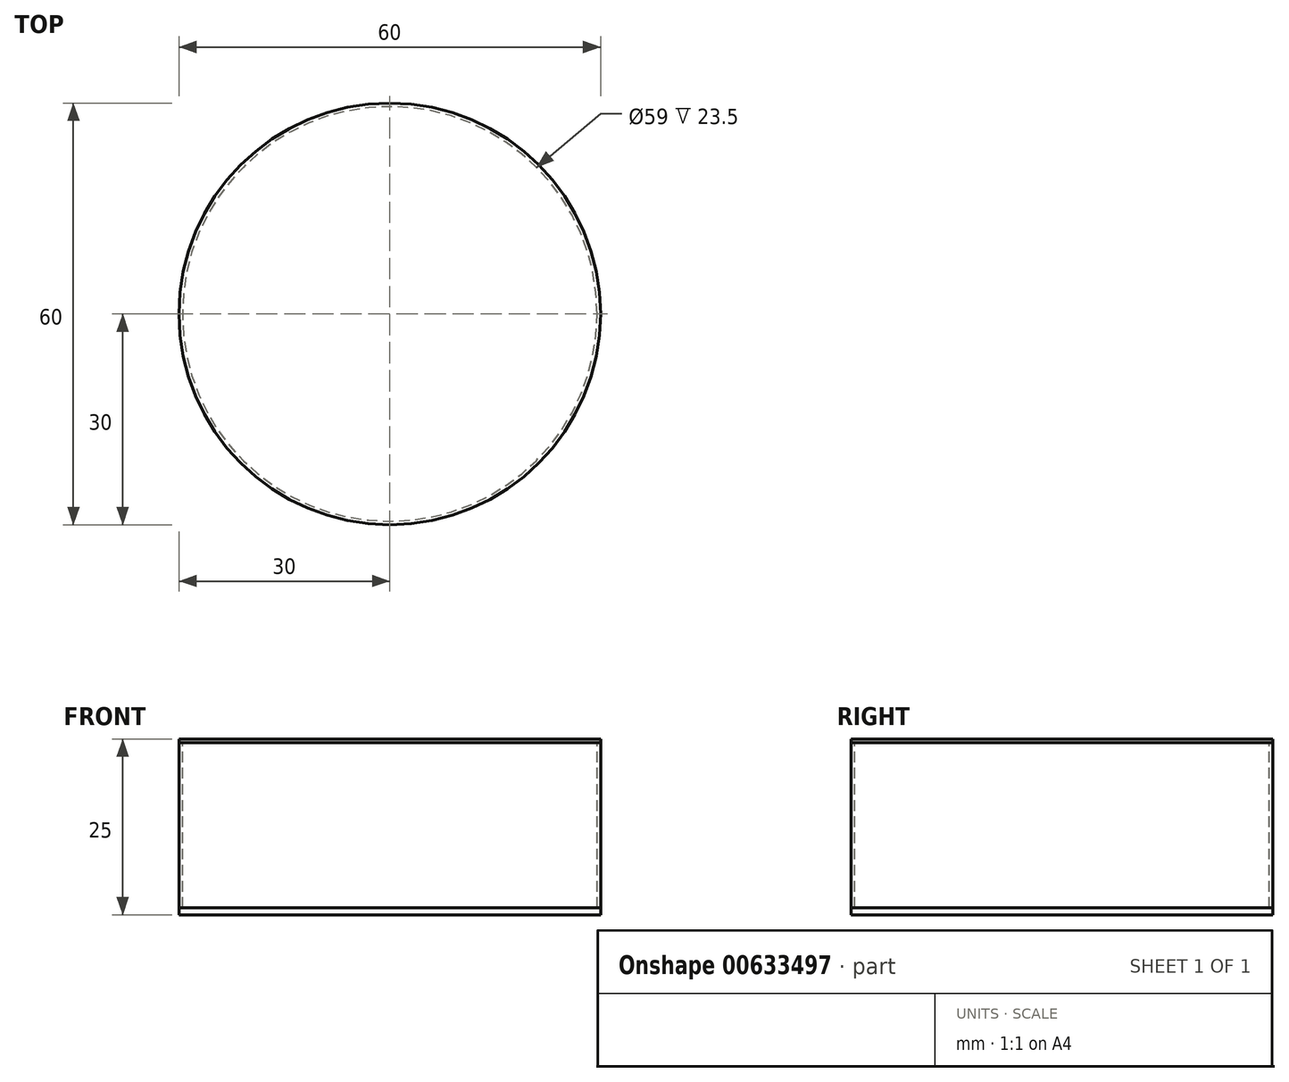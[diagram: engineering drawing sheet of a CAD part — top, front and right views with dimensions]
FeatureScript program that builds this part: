
annotation { "Feature Type Name" : "Feature", "Feature Type Description" : "" }
export const myFeature = defineFeature(function(context is Context, id is Id, definition is map)
    precondition{}
    {
        {
            var Q0;
            Q0=qCreatedBy(makeId("Top.planeOp"),FACE);
            var sketch = newSketch(context, id + "F0", { "sketchPlane" : qUnion([Q0])});
            skCircle(sketch, "E0", {"center": v(0, 0) * mm, "radius": 30 * mm});
            skSolve(sketch);
        }
        {
            var Q0;
            Q0=makeQuery(id+"F0.imprint","IMPRINT",FACE,{"disambiguationData":[TD([[makeQuery(id+"F0.imprint","IMPRINT",EDGE,{"derivedFrom":sQuery(id+"F0.wireOp",EDGE,"E0")}),1.0]])]});
            extrude(context, id + "F1", {"entities" : qUnion([Q0]), "oppositeDirection" : true, "depth" : .5 * mm, "offsetDistance" : 25 * mm});
        }
        {
            var Q0;
            Q0=qCreatedBy(makeId("Front.planeOp"),FACE);
            var sketch = newSketch(context, id + "F2", { "sketchPlane" : qUnion([Q0])});
            skLineSegment(sketch, "E1", {"start": v(0, 0) * mm, "end": v(0, -25) * mm, "construction": true});
            skLineSegment(sketch, "E2", {"start": v(0, -25) * mm, "end": v(30, -25) * mm});
            skLineSegment(sketch, "E3", {"start": v(30, -25) * mm, "end": v(30, -24) * mm});
            skLineSegment(sketch, "E4", {"start": v(30, -24) * mm, "end": v(0, -24) * mm});
            skLineSegment(sketch, "E5", {"start": v(0, -24) * mm, "end": v(0, -25) * mm});
            skSolve(sketch);
        }
        {
            var Q0;
            Q0=makeQuery(id+"F2.imprint","IMPRINT",FACE,{"disambiguationData":[TD([[makeQuery(id+"F2.imprint","IMPRINT",EDGE,{"derivedFrom":sQuery(id+"F2.wireOp",EDGE,"E2")}),1.0]])]});
            var Q1;
            Q1=sQuery(id+"F2.wireOp",EDGE,"E1");
            revolve(context, id + "F3", {"entities" : qUnion([Q0]), "axis" : qUnion([Q1]), "revolveType" : RevolveType.FULL});
        }
        {
            var Q0;
            Q0=makeQuery(id+"F1.opExtrude","CAP_FACE",FACE,{"disambiguationData":[OSD([sQuery(id+"F0.wireOp",EDGE,"E0")])],"isStart":false});
            var sketch = newSketch(context, id + "F4", { "sketchPlane" : qUnion([Q0])});
            skCircle(sketch, "E6", {"center": v(0, 0) * mm, "radius": 29.5 * mm});
            skSolve(sketch);
        }
        {
            var Q0;
            Q0=makeQuery(id+"F4.imprint","IMPRINT",FACE,{"disambiguationData":[TD([[makeQuery(id+"F4.imprint","IMPRINT",EDGE,{"derivedFrom":sQuery(id+"F4.wireOp",EDGE,"E6")}),-1.0]])]});
            var Q1;
            Q1=makeQuery(id+"F3.opRevolve","SWEPT_FACE",FACE,{"disambiguationData":[OSD([sQuery(id+"F2.wireOp",EDGE,"E4")])]});
            extrude(context, id + "F5", {"entities" : qUnion([Q0]), "endBound" : BoundingType.UP_TO_SURFACE, "depth" : 25 * mm, "endBoundEntityFace" : qUnion([Q1]), "offsetDistance" : 25 * mm});
        }
    });
